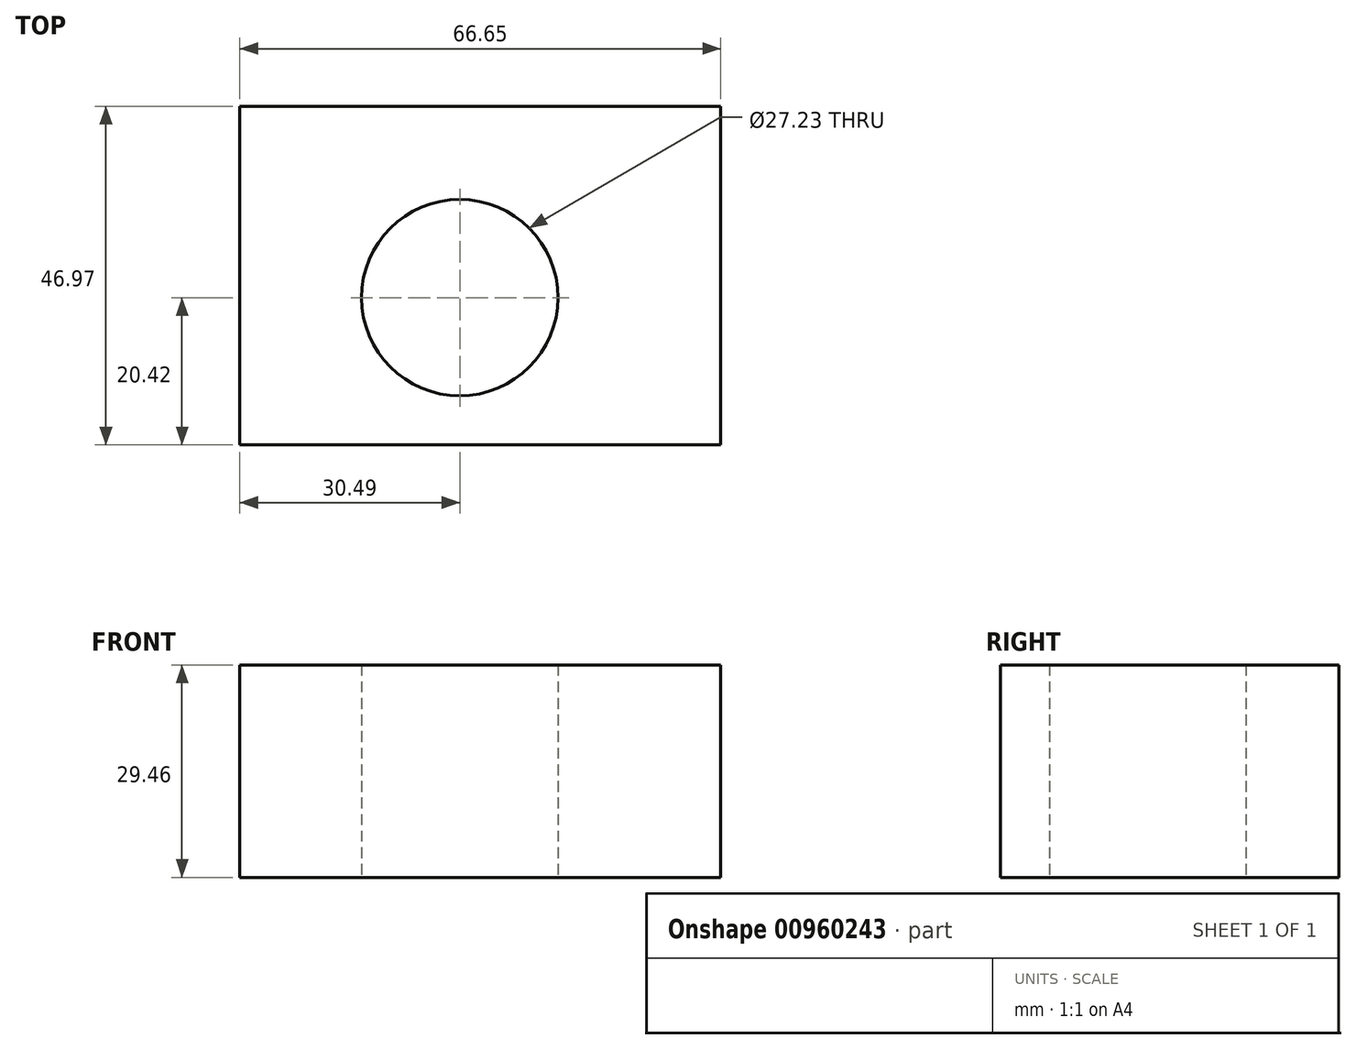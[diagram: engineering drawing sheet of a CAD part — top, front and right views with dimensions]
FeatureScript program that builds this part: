
annotation { "Feature Type Name" : "Feature", "Feature Type Description" : "" }
export const myFeature = defineFeature(function(context is Context, id is Id, definition is map)
    precondition{}
    {
        {
            var Q0;
            Q0=qCreatedBy(makeId("Top.planeOp"),FACE);
            var sketch = newSketch(context, id + "F0", { "sketchPlane" : qUnion([Q0])});
            skLineSegment(sketch, "E0.bottom", {"start": v(36.16, 26.55) * mm, "end": v(-30.49, 26.55) * mm});
            skLineSegment(sketch, "E0.top", {"start": v(36.16, -20.42) * mm, "end": v(-30.49, -20.42) * mm});
            skLineSegment(sketch, "E0.left", {"start": v(36.16, 26.55) * mm, "end": v(36.16, -20.42) * mm});
            skLineSegment(sketch, "E0.right", {"start": v(-30.49, 26.55) * mm, "end": v(-30.49, -20.42) * mm});
            skSolve(sketch);
        }
        {
            var Q0;
            Q0=qCreatedBy(makeId("Top.planeOp"),FACE);
            var sketch = newSketch(context, id + "F1", { "sketchPlane" : qUnion([Q0])});
            skCircle(sketch, "E1", {"center": v(0, 0) * mm, "radius": 13.61 * mm});
            skSolve(sketch);
        }
        {
            var Q0;
            Q0=makeQuery(id+"F0.imprint","IMPRINT",FACE,{"disambiguationData":[TD([[makeQuery(id+"F0.imprint","IMPRINT",EDGE,{"derivedFrom":sQuery(id+"F0.wireOp",EDGE,"E0.bottom")}),1.0]])]});
            extrude(context, id + "F2", {"entities" : qUnion([Q0]), "oppositeDirection" : true, "depth" : 29.46 * mm, "offsetDistance" : 25.4 * mm});
        }
        {
            var Q0;
            Q0=makeQuery(id+"F1.imprint","IMPRINT",FACE,{"disambiguationData":[TD([[makeQuery(id+"F1.imprint","IMPRINT",EDGE,{"derivedFrom":sQuery(id+"F1.wireOp",EDGE,"E1")}),1.0]])]});
            extrude(context, id + "F3", {"entities" : qUnion([Q0]), "operationType" : NewBodyOperationType.ADD, "oppositeDirection" : true, "depth" : 48.5 * mm, "offsetDistance" : 25.4 * mm});
        }
        {
            var Q0;
            Q0=makeQuery(id+"F3.opExtrude","CAP_FACE",FACE,{"disambiguationData":[OSD([sQuery(id+"F1.wireOp",EDGE,"E1")])],"isStart":false});
            extrude(context, id + "F4", {"entities" : qUnion([Q0]), "operationType" : NewBodyOperationType.REMOVE, "oppositeDirection" : true, "depth" : 84.84 * mm, "offsetDistance" : 25.4 * mm});
        }
    });
